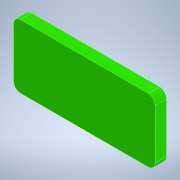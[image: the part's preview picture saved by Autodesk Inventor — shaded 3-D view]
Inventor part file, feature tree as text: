
AUTODESK INVENTOR PART (.ipt)
format: ipt  version: 2021 (Build 250183000, 183)  size: 125,440 bytes
history: native  units: mm
features: reference x29, other x4, extrude x1, fillet x1, sketch x1, projected_geometry x1
ambient origin geometry x8: Origin, YZ Plane, XZ Plane, XY Plane, X Axis, Y Axis, Z Axis, Center Point
bodies: Solid1 (feature_tree)
feature tree (37):
  extrude  "Extrusion1"  Depth=9.0mm
  fillet  "Fillet1"  Radius=1.6mm
  other  "MiniUSB_ADAPTER_PCB_OUTLINE"
  sketch  "Sketch1"  dims[d0=20.0mm d1=9.0mm d2=1.6mm d3=0.0mm d4=1.0mm]
  reference  "Reference1"
  reference  "Reference2"
  reference  "Reference3"
  reference  "Reference4"
  reference  "Reference5"
  reference  "Reference6"
  reference  "Reference7"
  reference  "Reference8"
  reference  "Reference9"
  reference  "Reference10"
  reference  "Reference11"
  reference  "Reference12"
  reference  "Reference13"
  reference  "Reference14"
  reference  "Reference15"
  reference  "Reference16"
  reference  "Reference17"
  reference  "Reference18"
  reference  "Reference19"
  reference  "Reference20"
  reference  "Reference21"
  reference  "Reference22"
  reference  "Reference23"
  reference  "Reference24"
  reference  "Reference25"
  reference  "Reference26"
  reference  "Reference27"
  reference  "Reference28"
  reference  "Reference29"
  projected_geometry  "Projected Loop1"
  other  "<userpath>\Google Drive\Unicorn 2020\CAD\Assembly.iam"
  other  "Assembly.iam"
  other  "M-MUSBR-B551-30-REVG1:1"
